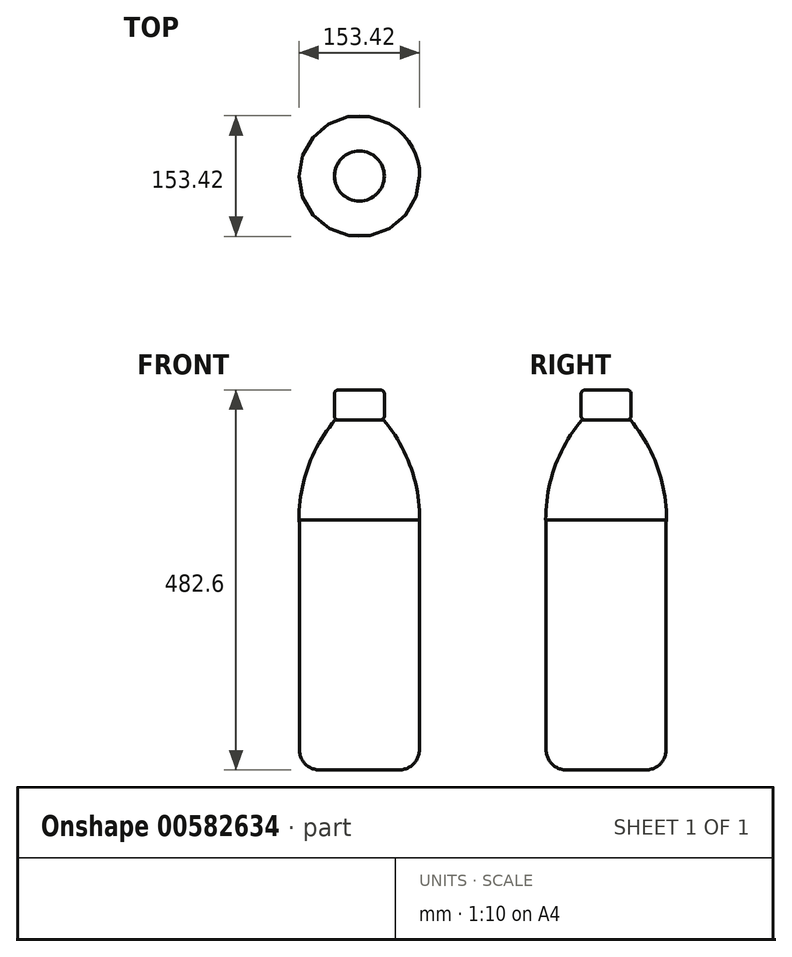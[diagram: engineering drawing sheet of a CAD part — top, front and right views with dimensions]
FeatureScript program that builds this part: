
annotation { "Feature Type Name" : "Feature", "Feature Type Description" : "" }
export const myFeature = defineFeature(function(context is Context, id is Id, definition is map)
    precondition{}
    {
        {
            var Q0;
            Q0=qCreatedBy(makeId("Front.planeOp"),FACE);
            var sketch = newSketch(context, id + "F0", { "sketchPlane" : qUnion([Q0])});
            skLineSegment(sketch, "E0", {"start": v(0, 0) * mm, "end": v(0, -317.5) * mm});
            skLineSegment(sketch, "E1", {"start": v(0, -317.5) * mm, "end": v(76.2, -317.5) * mm});
            skLineSegment(sketch, "E2", {"start": v(76.2, -317.5) * mm, "end": v(76.2, 0) * mm});
            skLineSegment(sketch, "E3", {"start": v(76.2, 0) * mm, "end": v(0, 0) * mm});
            skSolve(sketch);
        }
        {
            var Q0;
            Q0=makeQuery(id+"F0.imprint","IMPRINT",FACE,{"disambiguationData":[TD([[makeQuery(id+"F0.imprint","IMPRINT",EDGE,{"derivedFrom":sQuery(id+"F0.wireOp",EDGE,"E0")}),1.0]])]});
            var Q1;
            Q1=sQuery(id+"F0.wireOp",EDGE,"E0");
            revolve(context, id + "F1", {"entities" : qUnion([Q0]), "axis" : qUnion([Q1]), "revolveType" : RevolveType.FULL});
        }
        {
            var Q0;
            Q0=qCreatedBy(makeId("Front.planeOp"),FACE);
            var sketch = newSketch(context, id + "F2", { "sketchPlane" : qUnion([Q0])});
            skLineSegment(sketch, "E4.bottom", {"start": v(0, 165.1) * mm, "end": v(31.75, 165.1) * mm});
            skLineSegment(sketch, "E4.top", {"start": v(0, 127) * mm, "end": v(31.75, 127) * mm});
            skLineSegment(sketch, "E4.left", {"start": v(0, 165.1) * mm, "end": v(0, 127) * mm});
            skLineSegment(sketch, "E4.right", {"start": v(31.75, 165.1) * mm, "end": v(31.75, 127) * mm});
            skSolve(sketch);
        }
        {
            var Q0;
            Q0=makeQuery(id+"F2.imprint","IMPRINT",FACE,{"disambiguationData":[TD([[makeQuery(id+"F2.imprint","IMPRINT",EDGE,{"derivedFrom":sQuery(id+"F2.wireOp",EDGE,"E4.bottom")}),-1.0]])]});
            var Q1;
            Q1=sQuery(id+"F2.wireOp",EDGE,"E4.left");
            revolve(context, id + "F3", {"entities" : qUnion([Q0]), "axis" : qUnion([Q1]), "revolveType" : RevolveType.FULL});
        }
        {
            var Q0;
            Q0=qCreatedBy(makeId("Front.planeOp"),FACE);
            var sketch = newSketch(context, id + "F4", { "sketchPlane" : qUnion([Q0])});
            skLineSegment(sketch, "E5", {"start": v(0, 126.94) * mm, "end": v(0, 0) * mm});
            skLineSegment(sketch, "E6", {"start": v(0, 0) * mm, "end": v(76.7, 0) * mm});
            skArc(sketch, "E7", {"start": v(76.7, 0) * mm, "mid": v(65.04, 67.57) * mm, "end": v(30.72, 126.94) * mm});
            skLineSegment(sketch, "E8", {"start": v(30.72, 126.94) * mm, "end": v(0, 126.94) * mm});
            skSolve(sketch);
        }
        {
            var Q0;
            Q0=makeQuery(id+"F4.imprint","IMPRINT",FACE,{"disambiguationData":[TD([[makeQuery(id+"F4.imprint","IMPRINT",EDGE,{"derivedFrom":sQuery(id+"F4.wireOp",EDGE,"E5")}),1.0]])]});
            var Q1;
            Q1=sQuery(id+"F4.wireOp",EDGE,"E5");
            revolve(context, id + "F5", {"operationType" : NewBodyOperationType.ADD, "entities" : qUnion([Q0]), "axis" : qUnion([Q1]), "revolveType" : RevolveType.FULL});
        }
        {
            var Q0;
            Q0=makeQuery(id+"F1.opRevolve","SWEPT_FACE",FACE,{"disambiguationData":[OSD([sQuery(id+"F0.wireOp",EDGE,"E1")])]});
            var Q1;
            Q1=makeQuery(id+"F1.opRevolve","SWEPT_FACE",FACE,{"disambiguationData":[OSD([sQuery(id+"F0.wireOp",EDGE,"E2")])]});
            fillet(context, id + "F6", {"entities" : qUnion([Q0, Q1]), "radius" : 25.4 * mm, "tangentPropagation" : true, "allowEdgeOverflow" : false});
        }
        {
            var Q0;
            Q0=makeQuery(id+"F3.opRevolve","SWEPT_EDGE",EDGE,{"disambiguationData":[OSD([sQuery(id+"F2.wireOp",EDGE,"E4.bottom"),sQuery(id+"F2.wireOp",EDGE,"E4.right")])]});
            var Q1;
            Q1=makeQuery(id+"F3.opRevolve","SWEPT_FACE",FACE,{"disambiguationData":[OSD([sQuery(id+"F2.wireOp",EDGE,"E4.right")])]});
            var Q2;
            Q2=makeQuery(id+"F3.opRevolve","SWEPT_FACE",FACE,{"disambiguationData":[OSD([sQuery(id+"F2.wireOp",EDGE,"E4.bottom")])]});
            fillet(context, id + "F7", {"entities" : qUnion([Q0, Q1, Q2]), "radius" : 5.08 * mm, "tangentPropagation" : true, "allowEdgeOverflow" : false});
        }
    });
